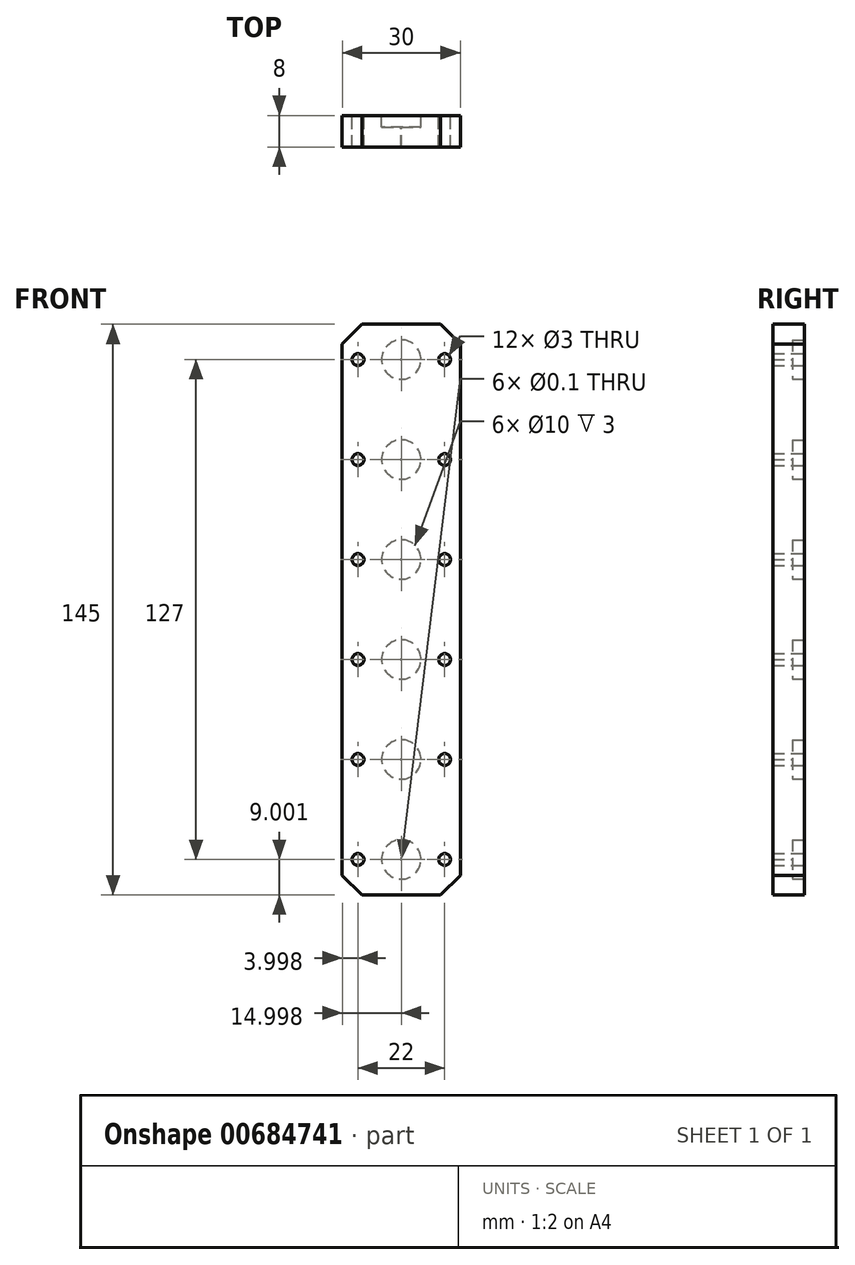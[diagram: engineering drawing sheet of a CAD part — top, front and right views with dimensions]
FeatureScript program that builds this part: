
annotation { "Feature Type Name" : "Feature", "Feature Type Description" : "" }
export const myFeature = defineFeature(function(context is Context, id is Id, definition is map)
    precondition{}
    {
        {
            var Q0;
            Q0=qCreatedBy(makeId("Front.planeOp"),FACE);
            var sketch = newSketch(context, id + "F0", { "sketchPlane" : qUnion([Q0])});
            skPoint(sketch, "E0", {"position": v(-5.65, 76.36) * mm});
            skPoint(sketch, "E0.positionSnap0", {"position": v(-5.65, 94.9) * mm});
            skPoint(sketch, "E1", {"position": v(-5.65, 50.96) * mm});
            skPoint(sketch, "E2", {"position": v(-5.65, 25.56) * mm});
            skPoint(sketch, "E3", {"position": v(-5.65, 0.16) * mm});
            skPoint(sketch, "E4", {"position": v(-5.65, -25.24) * mm});
            skPoint(sketch, "E5", {"position": v(-5.65, -50.64) * mm});
            skPoint(sketch, "E6", {"position": v(-16.65, 76.36) * mm});
            skPoint(sketch, "E7", {"position": v(-16.65, 50.96) * mm});
            skPoint(sketch, "E8", {"position": v(-16.65, 25.56) * mm});
            skPoint(sketch, "E9", {"position": v(-16.65, 0.16) * mm});
            skPoint(sketch, "E10", {"position": v(-16.65, -25.24) * mm});
            skPoint(sketch, "E11", {"position": v(-16.65, -50.64) * mm});
            skPoint(sketch, "E12", {"position": v(5.35, 76.36) * mm});
            skPoint(sketch, "E13", {"position": v(5.35, 50.96) * mm});
            skPoint(sketch, "E14", {"position": v(5.35, 25.56) * mm});
            skPoint(sketch, "E15", {"position": v(5.35, 0.16) * mm});
            skPoint(sketch, "E16", {"position": v(5.35, -25.24) * mm});
            skPoint(sketch, "E17", {"position": v(5.35, -50.64) * mm});
            skLineSegment(sketch, "E18", {"start": v(-20.65, 85.36) * mm, "end": v(9.35, 85.36) * mm});
            skPoint(sketch, "E19.endSnap0", {"position": v(-5.65, 85.36) * mm});
            skLineSegment(sketch, "E20", {"start": v(9.35, 85.36) * mm, "end": v(9.35, -59.64) * mm});
            skLineSegment(sketch, "E21", {"start": v(9.35, -59.64) * mm, "end": v(-20.65, -59.64) * mm});
            skLineSegment(sketch, "E22", {"start": v(-20.65, -59.64) * mm, "end": v(-20.65, 85.36) * mm});
            skSolve(sketch);
        }
        {
            var Q0;
            Q0=makeQuery(id+"F0.imprint","IMPRINT",FACE,{"disambiguationData":[TD([[makeQuery(id+"F0.imprint","IMPRINT",EDGE,{"derivedFrom":sQuery(id+"F0.wireOp",EDGE,"E18")}),-1.0]])]});
            extrude(context, id + "F1", {"entities" : qUnion([Q0]), "depth" : 8 * mm, "offsetDistance" : 25 * mm});
        }
        {
            var Q0;
            Q0=sQuery(id+"F0.wireOp",VERTEX,"E12");
            var Q1;
            Q1=sQuery(id+"F0.wireOp",VERTEX,"E13");
            var Q2;
            Q2=sQuery(id+"F0.wireOp",VERTEX,"E14");
            var Q3;
            Q3=sQuery(id+"F0.wireOp",VERTEX,"E15");
            var Q4;
            Q4=sQuery(id+"F0.wireOp",VERTEX,"E16");
            var Q5;
            Q5=sQuery(id+"F0.wireOp",VERTEX,"E17");
            var Q6;
            Q6=sQuery(id+"F0.wireOp",VERTEX,"E11");
            var Q7;
            Q7=sQuery(id+"F0.wireOp",VERTEX,"E10");
            var Q8;
            Q8=sQuery(id+"F0.wireOp",VERTEX,"E9");
            var Q9;
            Q9=sQuery(id+"F0.wireOp",VERTEX,"E8");
            var Q10;
            Q10=sQuery(id+"F0.wireOp",VERTEX,"E7");
            var Q11;
            Q11=sQuery(id+"F0.wireOp",VERTEX,"E6");
            var Q12;
            Q12=makeQuery(id+"F1.opExtrude","SWEPT_BODY",BODY,{"disambiguationData":[OSD([sQuery(id+"F0.wireOp",EDGE,"E18"),sQuery(id+"F0.wireOp",EDGE,"E20"),sQuery(id+"F0.wireOp",EDGE,"E21"),sQuery(id+"F0.wireOp",EDGE,"E22")])]});
            hole(context, id + "F2", {"style" : HoleStyle.SIMPLE, "endStyle" : HoleEndStyle.THROUGH, "oppositeDirection" : true, "holeDiameter" : 3 * mm, "majorDiameter" : 5 * mm, "isTappedThrough" : true, "tappedDepth" : 17.25 * mm, "tapClearance" : 3, "locations" : qUnion([Q0, Q1, Q2, Q3, Q4, Q5, Q6, Q7, Q8, Q9, Q10, Q11]), "scope" : qUnion([Q12])});
        }
        {
            var Q0;
            Q0=sQuery(id+"F0.wireOp",VERTEX,"E0");
            var Q1;
            Q1=sQuery(id+"F0.wireOp",VERTEX,"E1");
            var Q2;
            Q2=sQuery(id+"F0.wireOp",VERTEX,"E2");
            var Q3;
            Q3=sQuery(id+"F0.wireOp",VERTEX,"E3");
            var Q4;
            Q4=sQuery(id+"F0.wireOp",VERTEX,"E4");
            var Q5;
            Q5=sQuery(id+"F0.wireOp",VERTEX,"E5");
            var Q6;
            Q6=makeQuery(id+"F1.opExtrude","SWEPT_BODY",BODY,{"disambiguationData":[OSD([sQuery(id+"F0.wireOp",EDGE,"E18"),sQuery(id+"F0.wireOp",EDGE,"E20"),sQuery(id+"F0.wireOp",EDGE,"E21"),sQuery(id+"F0.wireOp",EDGE,"E22")])]});
            hole(context, id + "F3", {"style" : HoleStyle.C_BORE, "endStyle" : HoleEndStyle.BLIND, "oppositeDirection" : true, "holeDiameter" : .1 * mm, "cBoreDiameter" : 10 * mm, "cBoreDepth" : 3 * mm, "majorDiameter" : 5 * mm, "holeDepth" : 23 * mm, "isTappedThrough" : true, "tappedDepth" : 17.25 * mm, "tapClearance" : 3, "locations" : qUnion([Q0, Q1, Q2, Q3, Q4, Q5]), "scope" : qUnion([Q6])});
        }
        {
            var Q0;
            Q0=makeQuery(id+"F1.opExtrude","SWEPT_EDGE",EDGE,{"disambiguationData":[OSD([sQuery(id+"F0.wireOp",EDGE,"E20"),sQuery(id+"F0.wireOp",EDGE,"E21")])]});
            var Q1;
            Q1=makeQuery(id+"F1.opExtrude","SWEPT_EDGE",EDGE,{"disambiguationData":[OSD([sQuery(id+"F0.wireOp",EDGE,"E21"),sQuery(id+"F0.wireOp",EDGE,"E22")])]});
            var Q2;
            Q2=makeQuery(id+"F1.opExtrude","SWEPT_EDGE",EDGE,{"disambiguationData":[OSD([sQuery(id+"F0.wireOp",EDGE,"E18"),sQuery(id+"F0.wireOp",EDGE,"E22")])]});
            var Q3;
            Q3=makeQuery(id+"F1.opExtrude","SWEPT_EDGE",EDGE,{"disambiguationData":[OSD([sQuery(id+"F0.wireOp",EDGE,"E18"),sQuery(id+"F0.wireOp",EDGE,"E20")])]});
            chamfer(context, id + "F4", {"entities" : qUnion([Q0, Q1, Q2, Q3]), "width" : 5 * mm, "tangentPropagation" : true});
        }
    });
